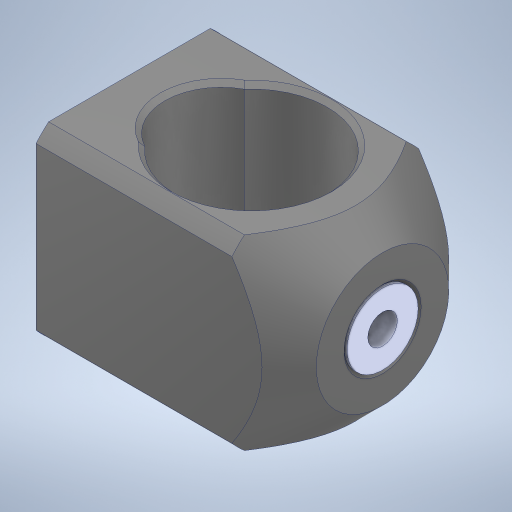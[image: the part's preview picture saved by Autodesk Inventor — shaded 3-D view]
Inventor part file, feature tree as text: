
AUTODESK INVENTOR PART (.ipt)
format: ipt  version: 2023 (Build 270158000, 158)  size: 295,424 bytes
history: mixed  units: in
note: dims shown in document units (in); Inventor stores cm internally (conversion verified against a paired STEP export)
features: extrude x3, sketch x3, other x1, imported_body x1
ambient origin geometry x8: Origin, YZ Plane, XZ Plane, XY Plane, X Axis, Y Axis, Z Axis, Center Point
bodies: Solid1 (imported_parasolid)
feature tree (8):
  other  "6669-001-1-solid1"
  extrude  "Extrusion1"  Depth=0.3937in
  sketch  "Sketch2"  dims[d8=0.3937in d9=0.0in d10=0.0in d11=0.0in]
  sketch  "Sketch3"  dims[d2=0.0197in d3=0.0344in d4=0.0197in d5=0.0344in]
  extrude  "Extrusion4"  TaperAngle=0.0deg  [1 undecoded]
  extrude  "Extrusion5"  Depth=0.0344in
  sketch  "Sketch1"  dims[d0=0.3937in d1=0.0in d7=0.0984in]
  imported_body  NMx_Import_Brep_tag  [imported B-rep: ~6 faces, bbox_mm=None]
note: 1 required parameter value undecoded (feature->parameter linkage not recoverable at this tier; creation-order binding heuristic only, values carry confidence <= 0.55)
